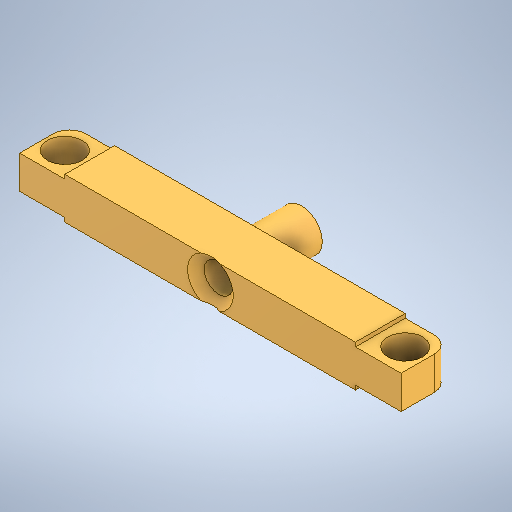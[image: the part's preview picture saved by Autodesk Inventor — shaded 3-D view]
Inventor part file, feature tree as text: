
AUTODESK INVENTOR PART (.ipt)
format: ipt  version: 2025.2 (Build 292293000, 293)  size: 310,272 bytes
history: native  units: in
note: dims shown in document units (in); Inventor stores cm internally (conversion verified against a paired STEP export)
features: extrude x3, sketch x3, other x1
ambient origin geometry x8: Origin, YZ Plane, XZ Plane, XY Plane, X Axis, Y Axis, Z Axis, Center Point
bodies: Solid1 (feature_tree)
feature tree (7):
  extrude  "Extrusion1"  Depth=0.1654in
  extrude  "Extrusion2"  Depth=0.2362in
  extrude  "Extrusion3"  Depth=0.2362in
  sketch  "Sketch1"  dims[d0=0.1654in d1=0.1654in]
  sketch  "Sketch2"  dims[d2=0.1969in d3=0.0in d4=0.2362in]
  sketch  "Sketch3"  dims[d5=0.2362in d6=0.2362in d7=0.2362in d8=0.0197in d9=0.0in d10=0.2362in d11=0.2362in d12=0.2362in d13=0.2362in d14=0.0197in d15=0.0in]
  other  "Com_MagnetMount"
